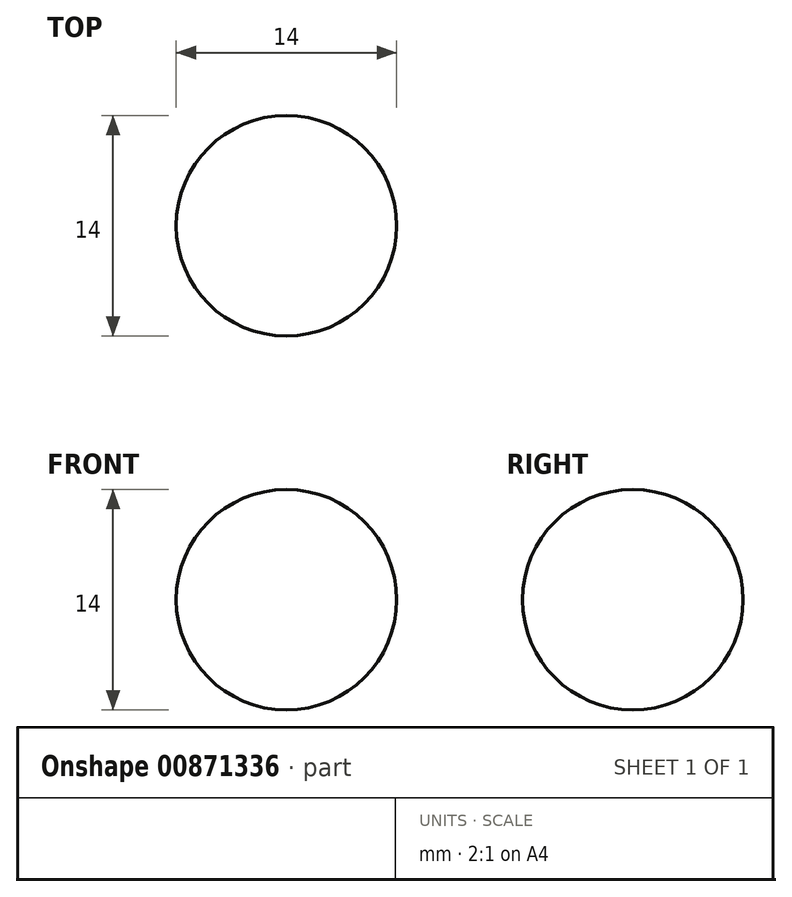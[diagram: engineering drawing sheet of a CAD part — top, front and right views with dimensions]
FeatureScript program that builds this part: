
annotation { "Feature Type Name" : "Feature", "Feature Type Description" : "" }
export const myFeature = defineFeature(function(context is Context, id is Id, definition is map)
    precondition{}
    {
        {
            var Q0;
            Q0=qCreatedBy(makeId("Front.planeOp"),FACE);
            var sketch = newSketch(context, id + "F0", { "sketchPlane" : qUnion([Q0])});
            skArc(sketch, "E0", {"start": v(0, 7) * mm, "mid": v(-7, 0) * mm, "end": v(0, -7) * mm});
            skLineSegment(sketch, "E1", {"start": v(0, 7) * mm, "end": v(0, -7) * mm});
            skSolve(sketch);
        }
        {
            var Q0;
            Q0 = qSketchRegion(id + "F0", true);
            var Q1;
            Q1=sQuery(id+"F0.wireOp",EDGE,"E1");
            revolve(context, id + "F1", {"surfaceOperationType" : NewSurfaceOperationType.NEW, "entities" : qUnion([Q0]), "axis" : qUnion([Q1]), "revolveType" : RevolveType.FULL});
        }
    });
